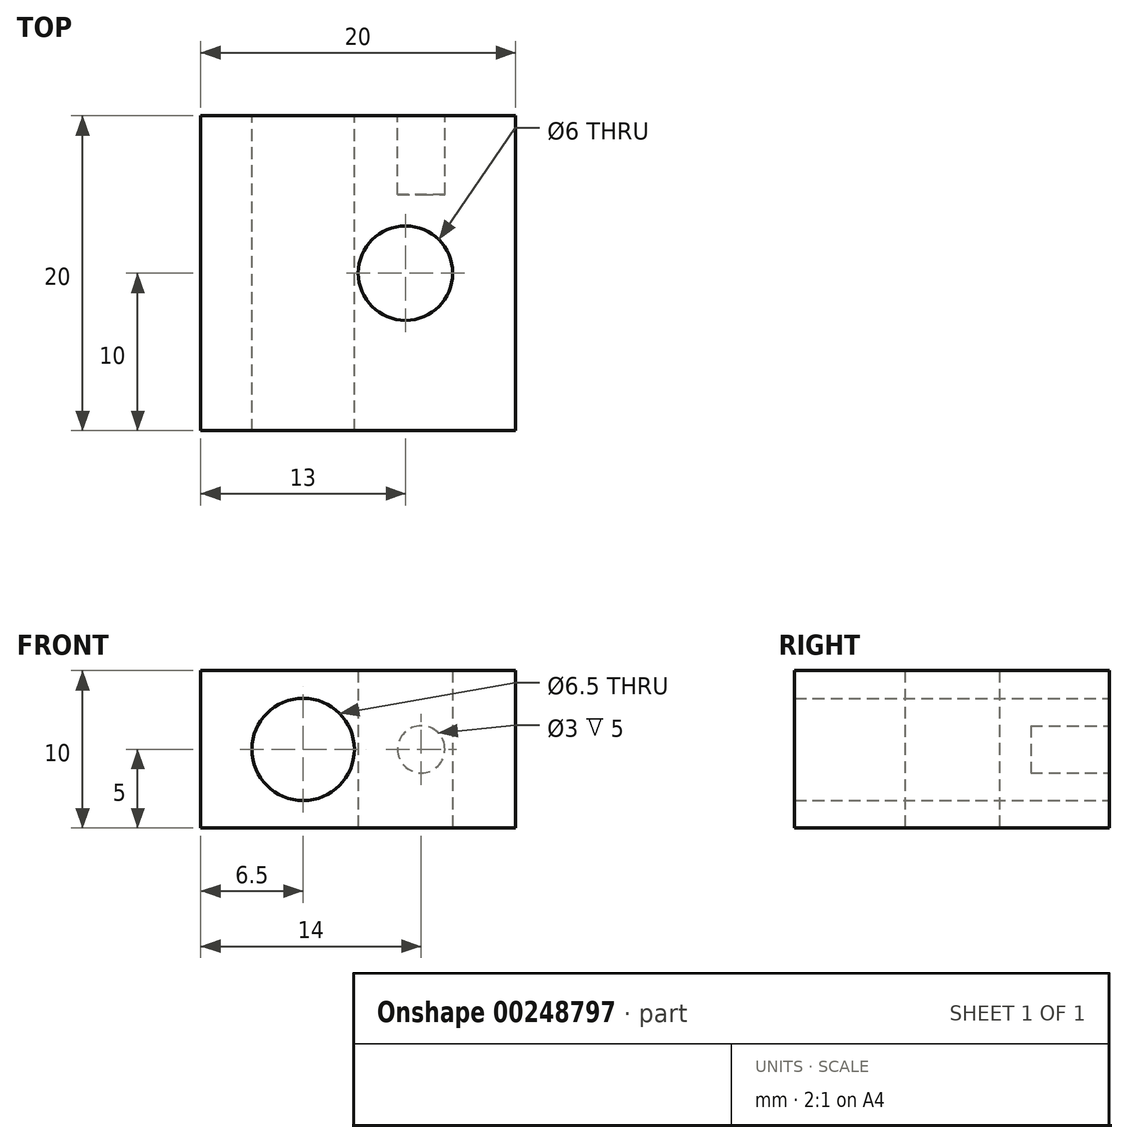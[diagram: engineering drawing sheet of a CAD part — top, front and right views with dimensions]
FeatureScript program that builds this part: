
annotation { "Feature Type Name" : "Feature", "Feature Type Description" : "" }
export const myFeature = defineFeature(function(context is Context, id is Id, definition is map)
    precondition{}
    {
        {
            var Q0;
            Q0=qCreatedBy(makeId("Top.planeOp"),FACE);
            var sketch = newSketch(context, id + "F0", { "sketchPlane" : qUnion([Q0])});
            skLineSegment(sketch, "E0.bottom", {"start": v(10, 10) * mm, "end": v(-10, 10) * mm});
            skLineSegment(sketch, "E0.top", {"start": v(10, -10) * mm, "end": v(-10, -10) * mm});
            skLineSegment(sketch, "E0.left", {"start": v(10, 10) * mm, "end": v(10, -10) * mm});
            skLineSegment(sketch, "E0.right", {"start": v(-10, 10) * mm, "end": v(-10, -10) * mm});
            skPoint(sketch, "E0.middle", {"position": v(0, 0) * mm});
            skCircle(sketch, "E1", {"center": v(3, 0) * mm, "radius": 3 * mm});
            skSolve(sketch);
        }
        {
            var Q0;
            Q0=makeQuery(id+"F0.imprint","IMPRINT",FACE,{"disambiguationData":[TD([[makeQuery(id+"F0.imprint","IMPRINT",EDGE,{"derivedFrom":sQuery(id+"F0.wireOp",EDGE,"E0.bottom")}),1.0]])]});
            extrude(context, id + "F1", {"entities" : qUnion([Q0]), "depth" : 10 * mm, "offsetDistance" : 25 * mm});
        }
        {
            var Q0;
            Q0=makeQuery(id+"F1.opExtrude","SWEPT_FACE",FACE,{"disambiguationData":[OSD([sQuery(id+"F0.wireOp",EDGE,"E0.bottom")])]});
            var sketch = newSketch(context, id + "F2", { "sketchPlane" : qUnion([Q0])});
            skCircle(sketch, "E2", {"center": v(3.5, 5) * mm, "radius": 3.25 * mm});
            skPoint(sketch, "E2.centerSnap0", {"position": v(10, 5) * mm});
            skCircle(sketch, "E3", {"center": v(-4, 5) * mm, "radius": 1.5 * mm});
            skSolve(sketch);
        }
        {
            var Q0;
            Q0=makeQuery(id+"F2.imprint","IMPRINT",FACE,{"disambiguationData":[TD([[makeQuery(id+"F2.imprint","IMPRINT",EDGE,{"derivedFrom":sQuery(id+"F2.wireOp",EDGE,"E2")}),1.0]])]});
            extrude(context, id + "F3", {"entities" : qUnion([Q0]), "operationType" : NewBodyOperationType.REMOVE, "endBound" : BoundingType.THROUGH_ALL, "oppositeDirection" : true, "depth" : 25 * mm, "offsetDistance" : 25 * mm});
        }
        {
            var Q0;
            Q0=makeQuery(id+"F2.imprint","IMPRINT",FACE,{"disambiguationData":[TD([[makeQuery(id+"F2.imprint","IMPRINT",EDGE,{"derivedFrom":sQuery(id+"F2.wireOp",EDGE,"E3")}),1.0]])]});
            extrude(context, id + "F4", {"entities" : qUnion([Q0]), "operationType" : NewBodyOperationType.REMOVE, "oppositeDirection" : true, "depth" : 5 * mm, "offsetDistance" : 25 * mm});
        }
    });
